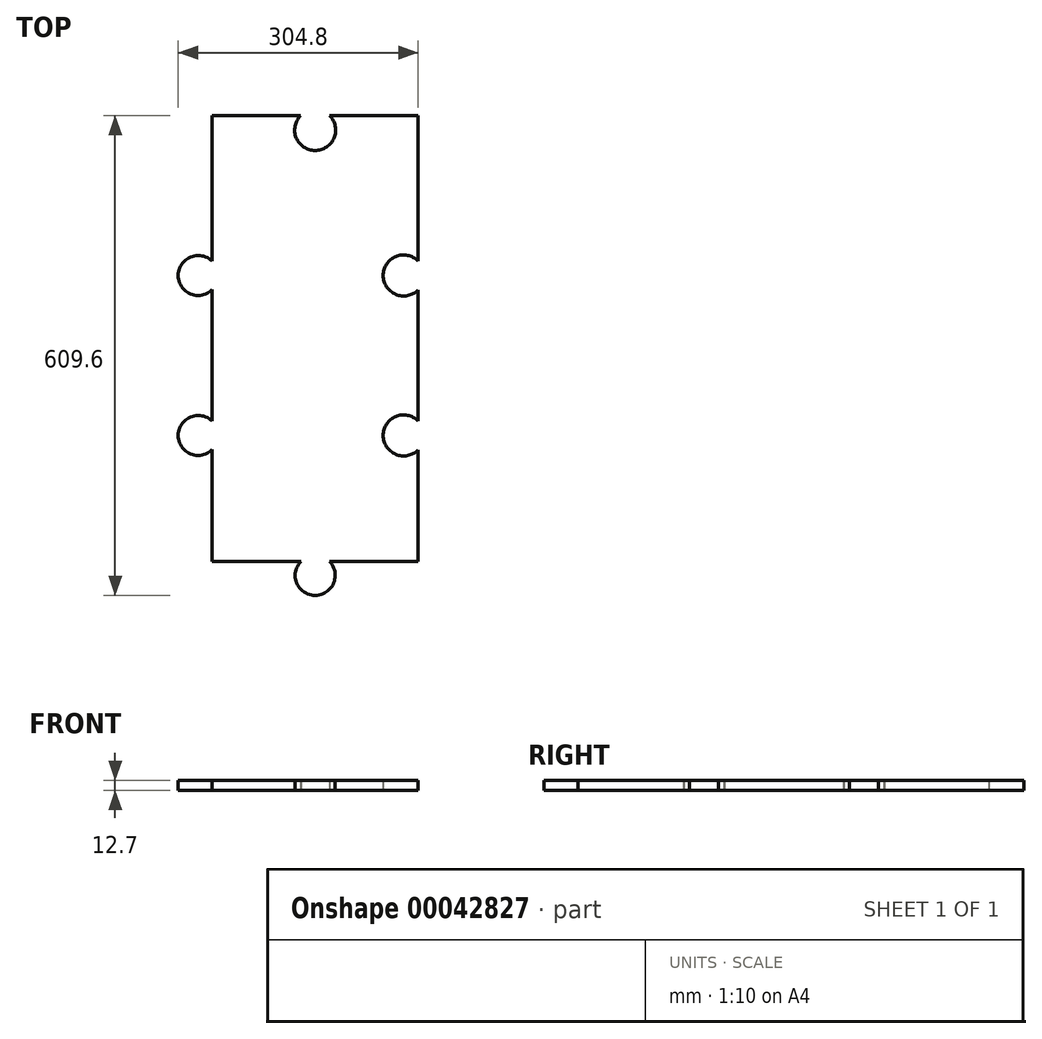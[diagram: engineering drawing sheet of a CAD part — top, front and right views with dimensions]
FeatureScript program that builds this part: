
annotation { "Feature Type Name" : "Feature", "Feature Type Description" : "" }
export const myFeature = defineFeature(function(context is Context, id is Id, definition is map)
    precondition{}
    {
        {
            var Q0;
            Q0=qCreatedBy(makeId("Top.planeOp"),FACE);
            var sketch = newSketch(context, id + "F0", { "sketchPlane" : qUnion([Q0])});
            skLineSegment(sketch, "E0.top", {"start": v(0, 566.42) * mm, "end": v(43.18, 566.42) * mm, "construction": true});
            skLineSegment(sketch, "E0.left", {"start": v(0, 0) * mm, "end": v(0, 566.42) * mm, "construction": true});
            skLineSegment(sketch, "E0.right", {"start": v(304.8, 0) * mm, "end": v(304.8, 141.62) * mm});
            skLineSegment(sketch, "E1", {"start": v(173.99, 566.42) * mm, "end": v(174, -43.18) * mm, "construction": true});
            skLineSegment(sketch, "E2", {"start": v(304.8, 363.22) * mm, "end": v(0, 363.22) * mm, "construction": true});
            skLineSegment(sketch, "E3", {"start": v(0, 160.02) * mm, "end": v(304.8, 160.02) * mm, "construction": true});
            skLineSegment(sketch, "E4", {"start": v(0, 0) * mm, "end": v(43.18, 0) * mm, "construction": true});
            skLineSegment(sketch, "E5", {"start": v(173.99, 566.42) * mm, "end": v(192.4, 566.42) * mm, "construction": true});
            skArc(sketch, "E6", {"start": v(155.85, 0) * mm, "mid": v(174, -43.18) * mm, "end": v(192.13, 0) * mm});
            skArc(sketch, "E7", {"start": v(192.13, 0) * mm, "mid": v(174, 7.62) * mm, "end": v(155.85, 0) * mm, "construction": true});
            skLineSegment(sketch, "E8", {"start": v(192.13, 0) * mm, "end": v(304.8, 0) * mm});
            skLineSegment(sketch, "E9", {"start": v(155.85, 0) * mm, "end": v(192.13, 0) * mm, "construction": true});
            skLineSegment(sketch, "E10", {"start": v(43.18, 566.42) * mm, "end": v(43.18, 381.36) * mm});
            skArc(sketch, "E11", {"start": v(304.8, 381.62) * mm, "mid": v(260.35, 363.22) * mm, "end": v(304.8, 344.82) * mm});
            skArc(sketch, "E12", {"start": v(304.8, 344.82) * mm, "mid": v(312.42, 363.22) * mm, "end": v(304.8, 381.62) * mm, "construction": true});
            skLineSegment(sketch, "E13", {"start": v(304.8, 381.62) * mm, "end": v(304.8, 566.42) * mm});
            skLineSegment(sketch, "E14", {"start": v(304.8, 344.82) * mm, "end": v(304.8, 381.62) * mm, "construction": true});
            skArc(sketch, "E15", {"start": v(304.8, 178.42) * mm, "mid": v(260.35, 160.02) * mm, "end": v(304.8, 141.62) * mm});
            skArc(sketch, "E16", {"start": v(304.8, 141.62) * mm, "mid": v(312.42, 160.02) * mm, "end": v(304.8, 178.42) * mm, "construction": true});
            skLineSegment(sketch, "E17", {"start": v(304.8, 178.42) * mm, "end": v(304.8, 344.82) * mm});
            skLineSegment(sketch, "E18", {"start": v(304.8, 141.62) * mm, "end": v(304.8, 178.42) * mm, "construction": true});
            skLineSegment(sketch, "E19", {"start": v(43.18, 566.42) * mm, "end": v(155.59, 566.42) * mm});
            skArc(sketch, "E20", {"start": v(43.18, 178.16) * mm, "mid": v(0, 160.02) * mm, "end": v(43.18, 141.88) * mm});
            skArc(sketch, "E21", {"start": v(43.18, 141.88) * mm, "mid": v(50.8, 160.02) * mm, "end": v(43.18, 178.16) * mm, "construction": true});
            skLineSegment(sketch, "E22", {"start": v(43.18, 141.88) * mm, "end": v(43.18, 0) * mm});
            skLineSegment(sketch, "E23", {"start": v(43.18, 178.16) * mm, "end": v(43.18, 141.88) * mm, "construction": true});
            skArc(sketch, "E24", {"start": v(43.18, 381.36) * mm, "mid": v(0, 363.22) * mm, "end": v(43.18, 345.08) * mm});
            skArc(sketch, "E25", {"start": v(43.18, 345.08) * mm, "mid": v(50.8, 363.22) * mm, "end": v(43.18, 381.36) * mm, "construction": true});
            skLineSegment(sketch, "E26", {"start": v(43.18, 345.08) * mm, "end": v(43.18, 178.16) * mm});
            skLineSegment(sketch, "E27", {"start": v(43.18, 381.36) * mm, "end": v(43.18, 345.08) * mm, "construction": true});
            skLineSegment(sketch, "E28", {"start": v(155.59, 566.42) * mm, "end": v(173.99, 566.42) * mm, "construction": true});
            skLineSegment(sketch, "E29", {"start": v(192.4, 566.42) * mm, "end": v(304.8, 566.42) * mm});
            skArc(sketch, "E30", {"start": v(192.4, 566.42) * mm, "mid": v(173.99, 574.04) * mm, "end": v(155.59, 566.42) * mm, "construction": true});
            skArc(sketch, "E31", {"start": v(155.59, 566.42) * mm, "mid": v(173.99, 521.97) * mm, "end": v(192.4, 566.42) * mm});
            skLineSegment(sketch, "E32", {"start": v(43.18, 0) * mm, "end": v(155.85, 0) * mm});
            skSolve(sketch);
        }
        {
            var Q0;
            Q0=makeQuery(id+"F0.imprint","IMPRINT",FACE,{"disambiguationData":[TD([[makeQuery(id+"F0.imprint","IMPRINT",EDGE,{"derivedFrom":sQuery(id+"F0.wireOp",EDGE,"E0.right")}),1.0]])]});
            extrude(context, id + "F1", {"entities" : qUnion([Q0]), "depth" : 12.7 * mm});
        }
    });
